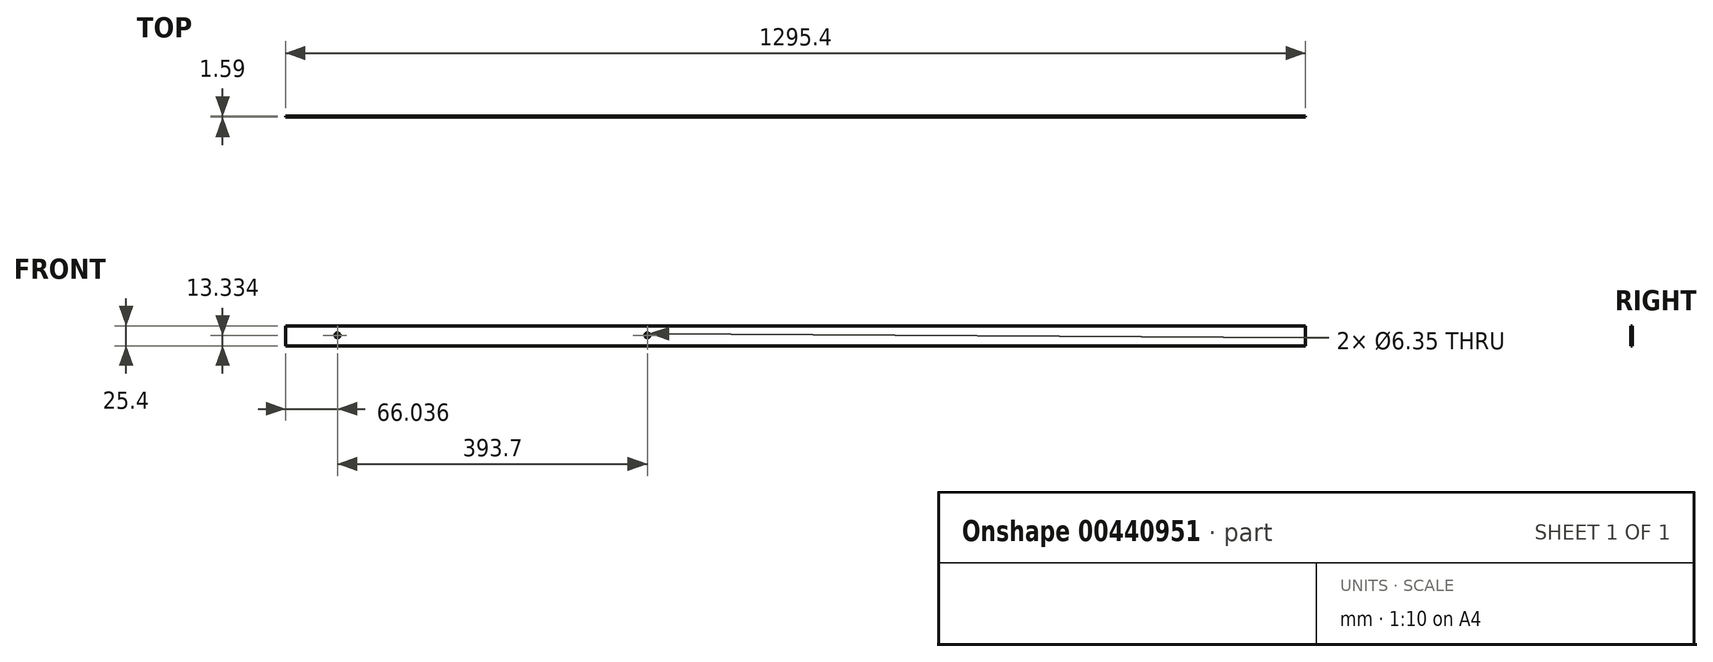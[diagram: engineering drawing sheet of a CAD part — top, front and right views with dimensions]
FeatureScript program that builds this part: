
annotation { "Feature Type Name" : "Feature", "Feature Type Description" : "" }
export const myFeature = defineFeature(function(context is Context, id is Id, definition is map)
    precondition{}
    {
        {
            var Q0;
            Q0=qCreatedBy(makeId("Front.planeOp"),FACE);
            var sketch = newSketch(context, id + "F0", { "sketchPlane" : qUnion([Q0])});
            skLineSegment(sketch, "E0.bottom", {"start": v(-644.6, -45.6) * mm, "end": v(650.8, -45.6) * mm});
            skLineSegment(sketch, "E0.top", {"start": v(-644.6, -71) * mm, "end": v(650.8, -71) * mm});
            skLineSegment(sketch, "E0.left", {"start": v(-644.6, -45.6) * mm, "end": v(-644.6, -71) * mm});
            skLineSegment(sketch, "E0.right", {"start": v(650.8, -45.6) * mm, "end": v(650.8, -71) * mm});
            skPoint(sketch, "E1", {"position": v(-578.55, -57.66) * mm});
            skPoint(sketch, "E2", {"position": v(-184.85, -57.66) * mm});
            skPoint(sketch, "E3", {"position": v(208.85, -57.66) * mm});
            skPoint(sketch, "E4", {"position": v(611.44, -57.66) * mm});
            skCircle(sketch, "E5", {"center": v(-578.55, -57.66) * mm, "radius": 3.18 * mm});
            skCircle(sketch, "E6", {"center": v(-184.85, -57.66) * mm, "radius": 3.18 * mm});
            skSolve(sketch);
        }
        {
            var Q0;
            Q0 = qSketchRegion(id + "F0", true);
            extrude(context, id + "F1", {"entities" : qUnion([Q0]), "depth" : 1.59 * mm});
        }
    });
